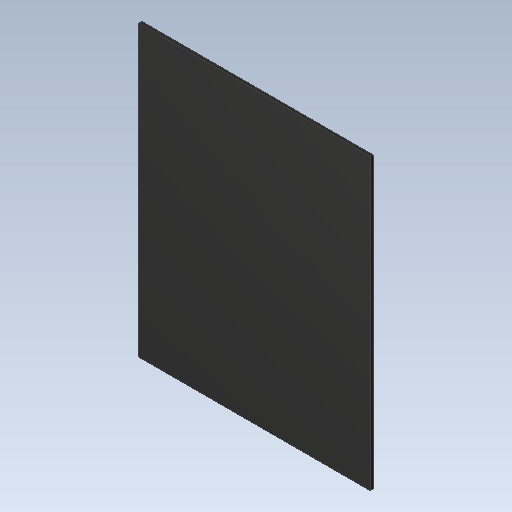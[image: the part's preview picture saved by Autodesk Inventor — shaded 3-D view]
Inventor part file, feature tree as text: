
AUTODESK INVENTOR PART (.ipt)
format: ipt  version: 2020 (Build 240168000, 168)  size: 86,016 bytes
history: imported  units: in
note: dims shown in document units (in); Inventor stores cm internally (conversion verified against a paired STEP export)
features: imported_body x1
ambient origin geometry x8: Origin, YZ Plane, XZ Plane, XY Plane, X Axis, Y Axis, Z Axis, Center Point
bodies: Solid1 (imported_parasolid), Body1 (imported_parasolid)
feature tree (1):
  imported_body  NMx_Import_Brep_tag  [imported B-rep: ~6 faces, bbox_mm=[8.191, 10.25, 0.1]]
